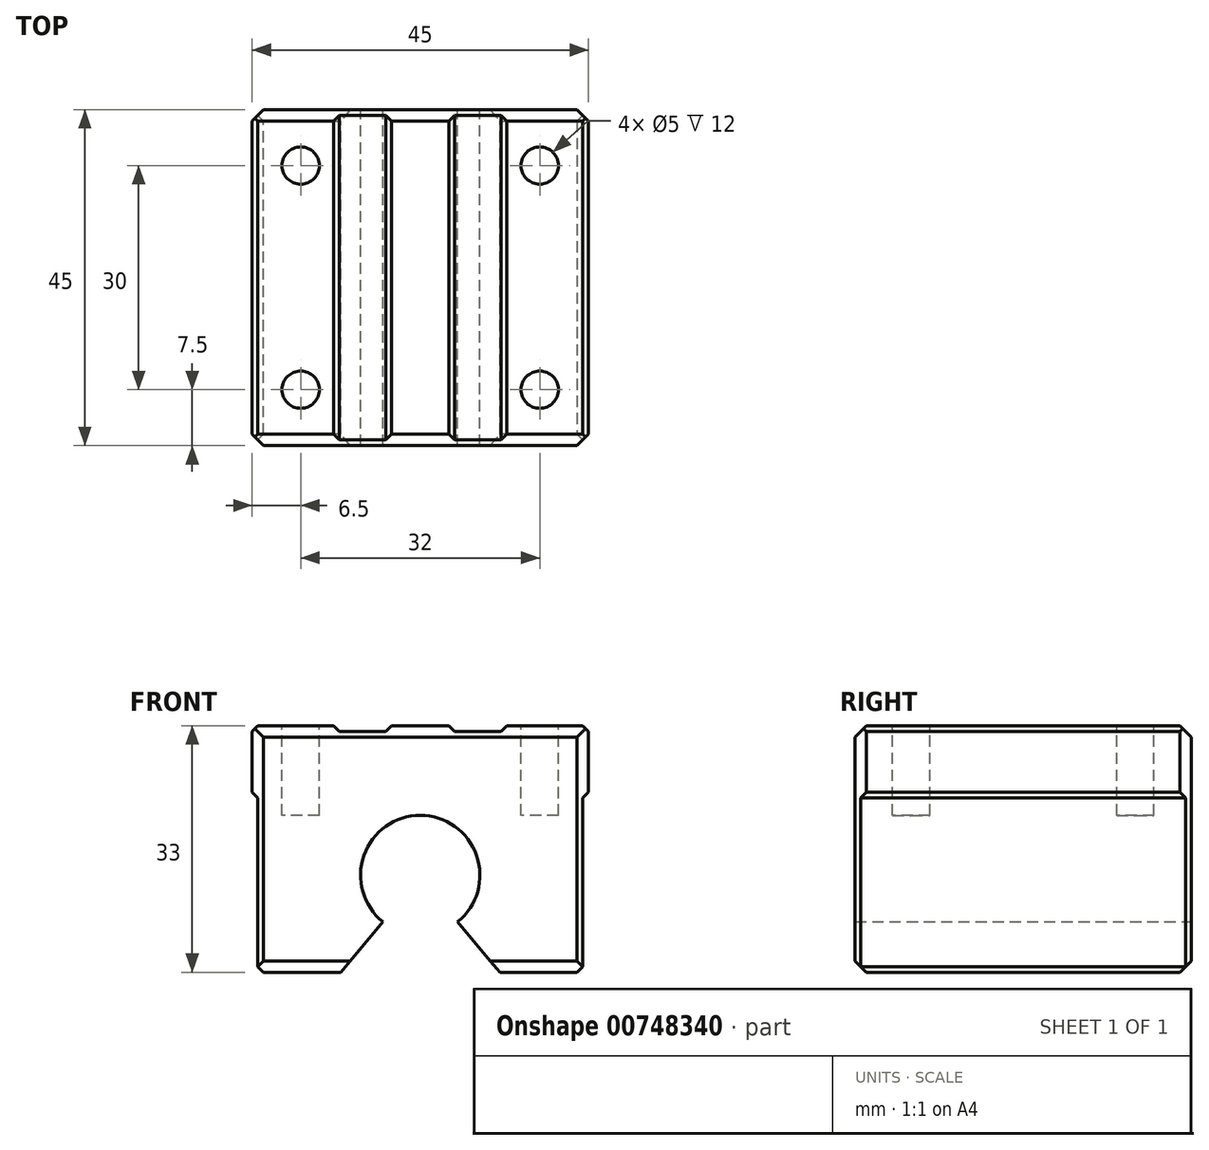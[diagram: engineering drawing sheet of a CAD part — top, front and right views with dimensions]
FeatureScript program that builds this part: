
annotation { "Feature Type Name" : "Feature", "Feature Type Description" : "" }
export const myFeature = defineFeature(function(context is Context, id is Id, definition is map)
    precondition{}
    {
        {
            var Q0;
            Q0=qCreatedBy(makeId("Front.planeOp"),FACE);
            var sketch = newSketch(context, id + "F0", { "sketchPlane" : qUnion([Q0])});
            skPoint(sketch, "E0.middle", {"position": v(0, 0) * mm});
            skLineSegment(sketch, "E1", {"start": v(-22.5, 15.23) * mm, "end": v(-22.5, 7.5) * mm});
            skLineSegment(sketch, "E2", {"start": v(-21.74, 6.82) * mm, "end": v(-21.74, -15.23) * mm});
            skLineSegment(sketch, "E3", {"start": v(-21.23, 16.5) * mm, "end": v(-11.72, 16.5) * mm});
            skLineSegment(sketch, "E4", {"start": v(-10.83, 15.74) * mm, "end": v(-4.58, 15.74) * mm});
            skLineSegment(sketch, "E5", {"start": v(-3.62, 16.5) * mm, "end": v(0, 16.5) * mm});
            skLineSegment(sketch, "E6", {"start": v(0, 16.5) * mm, "end": v(0, -16.5) * mm, "construction": true});
            skLineSegment(sketch, "E7.0", {"start": v(-5, 16.5) * mm, "end": v(-5, -16.5) * mm, "construction": true});
            skLineSegment(sketch, "E8.0", {"start": v(0, -3.5) * mm, "end": v(-21.23, -3.5) * mm, "construction": true});
            skLineSegment(sketch, "E9", {"start": v(-10.67, -16.5) * mm, "end": v(-5, -9.74) * mm});
            skLineSegment(sketch, "E10", {"start": v(0, 16.5) * mm, "end": v(0, 4.5) * mm});
            skArc(sketch, "E11", {"start": v(0, 4.5) * mm, "mid": v(-7.53, -0.86) * mm, "end": v(-5, -9.74) * mm});
            skLineSegment(sketch, "E12", {"start": v(-22.5, 7.5) * mm, "end": v(-22.5, 6.82) * mm});
            skLineSegment(sketch, "E13", {"start": v(-22.5, 6.82) * mm, "end": v(-21.74, 6.82) * mm});
            skLineSegment(sketch, "E14", {"start": v(-21.74, -15.23) * mm, "end": v(-21.74, -16.5) * mm});
            skLineSegment(sketch, "E15", {"start": v(-21.74, -16.5) * mm, "end": v(-20.53, -16.5) * mm});
            skLineSegment(sketch, "E16", {"start": v(-22.5, 15.23) * mm, "end": v(-22.5, 16.5) * mm});
            skLineSegment(sketch, "E17", {"start": v(-22.5, 16.5) * mm, "end": v(-21.23, 16.5) * mm});
            skLineSegment(sketch, "E18", {"start": v(-10.83, 15.74) * mm, "end": v(-10.83, 16.5) * mm});
            skLineSegment(sketch, "E19", {"start": v(-10.83, 16.5) * mm, "end": v(-11.72, 16.5) * mm});
            skLineSegment(sketch, "E20", {"start": v(-4.58, 15.74) * mm, "end": v(-4.58, 16.5) * mm});
            skLineSegment(sketch, "E21", {"start": v(-4.58, 16.5) * mm, "end": v(-3.62, 16.5) * mm});
            skLineSegment(sketch, "E22.MirrorCS", {"start": v(3.62, 16.5) * mm, "end": v(0, 16.5) * mm});
            skLineSegment(sketch, "E23.MirrorCS", {"start": v(4.58, 16.5) * mm, "end": v(3.62, 16.5) * mm});
            skLineSegment(sketch, "E24.MirrorCS", {"start": v(4.58, 15.74) * mm, "end": v(4.58, 16.5) * mm});
            skLineSegment(sketch, "E25.MirrorCS", {"start": v(10.83, 15.74) * mm, "end": v(4.58, 15.74) * mm});
            skLineSegment(sketch, "E26.MirrorCS", {"start": v(10.83, 15.74) * mm, "end": v(10.83, 16.5) * mm});
            skLineSegment(sketch, "E27.MirrorCS", {"start": v(10.83, 16.5) * mm, "end": v(11.72, 16.5) * mm});
            skLineSegment(sketch, "E28.MirrorCS", {"start": v(21.23, 16.5) * mm, "end": v(11.72, 16.5) * mm});
            skLineSegment(sketch, "E29.MirrorCS", {"start": v(22.5, 16.5) * mm, "end": v(21.23, 16.5) * mm});
            skLineSegment(sketch, "E30.MirrorCS", {"start": v(22.5, 15.23) * mm, "end": v(22.5, 16.5) * mm});
            skLineSegment(sketch, "E31.MirrorCS", {"start": v(22.5, 15.23) * mm, "end": v(22.5, 7.5) * mm});
            skLineSegment(sketch, "E32.MirrorCS", {"start": v(22.5, 7.5) * mm, "end": v(22.5, 6.82) * mm});
            skLineSegment(sketch, "E33.MirrorCS", {"start": v(22.5, 6.82) * mm, "end": v(21.74, 6.82) * mm});
            skLineSegment(sketch, "E34.MirrorCS", {"start": v(21.74, 6.82) * mm, "end": v(21.74, -15.23) * mm});
            skLineSegment(sketch, "E35.MirrorCS", {"start": v(21.74, -15.23) * mm, "end": v(21.74, -16.5) * mm});
            skLineSegment(sketch, "E36.MirrorCS", {"start": v(21.74, -16.5) * mm, "end": v(20.53, -16.5) * mm});
            skLineSegment(sketch, "E37", {"start": v(-20.53, -16.5) * mm, "end": v(-10.67, -16.5) * mm});
            skLineSegment(sketch, "E38.MirrorCS", {"start": v(20.53, -16.5) * mm, "end": v(10.67, -16.5) * mm});
            skLineSegment(sketch, "E39.MirrorCS", {"start": v(10.67, -16.5) * mm, "end": v(5, -9.74) * mm});
            skArc(sketch, "E40.MirrorCS", {"start": v(0, 4.5) * mm, "mid": v(7.53, -0.86) * mm, "end": v(5, -9.74) * mm});
            skSolve(sketch);
        }
        {
            var Q0;
            Q0=makeQuery(id+"F0.imprint","IMPRINT",FACE,{"disambiguationData":[TD([[makeQuery(id+"F0.imprint","IMPRINT",EDGE,{"derivedFrom":sQuery(id+"F0.wireOp",EDGE,"E10")}),1.0]])]});
            var Q1;
            Q1=makeQuery(id+"F0.imprint","IMPRINT",FACE,{"disambiguationData":[TD([[makeQuery(id+"F0.imprint","IMPRINT",EDGE,{"derivedFrom":sQuery(id+"F0.wireOp",EDGE,"E1")}),1.0]])]});
            extrude(context, id + "F1", {"entities" : qUnion([Q0, Q1]), "depth" : 45 * mm, "offsetDistance" : 25.4 * mm});
        }
        {
            var Q0;
            Q0=makeQuery(id+"F1.opExtrude","SWEPT_EDGE",EDGE,{"disambiguationData":[OSD([sQuery(id+"F0.wireOp",EDGE,"E16"),sQuery(id+"F0.wireOp",EDGE,"E17")])]});
            chamfer(context, id + "F2", {"entities" : qUnion([Q0]), "chamferType" : ChamferType.OFFSET_ANGLE, "width" : 0.76 * mm, "oppositeDirection" : false, "angle" : 45 * degree, "tangentPropagation" : true});
        }
        {
            var Q0;
            Q0=makeQuery(id+"F1.opExtrude","SWEPT_EDGE",EDGE,{"disambiguationData":[OSD([sQuery(id+"F0.wireOp",EDGE,"E18"),sQuery(id+"F0.wireOp",EDGE,"E19")])]});
            var Q1;
            Q1=makeQuery(id+"F1.opExtrude","SWEPT_EDGE",EDGE,{"disambiguationData":[OSD([sQuery(id+"F0.wireOp",EDGE,"E20"),sQuery(id+"F0.wireOp",EDGE,"E21")])]});
            var Q2;
            Q2=makeQuery(id+"F1.opExtrude","SWEPT_EDGE",EDGE,{"disambiguationData":[OSD([sQuery(id+"F0.wireOp",EDGE,"E23.MirrorCS"),sQuery(id+"F0.wireOp",EDGE,"E24.MirrorCS")])]});
            var Q3;
            Q3=makeQuery(id+"F1.opExtrude","SWEPT_EDGE",EDGE,{"disambiguationData":[OSD([sQuery(id+"F0.wireOp",EDGE,"E26.MirrorCS"),sQuery(id+"F0.wireOp",EDGE,"E27.MirrorCS")])]});
            var Q4;
            Q4=makeQuery(id+"F1.opExtrude","SWEPT_EDGE",EDGE,{"disambiguationData":[OSD([sQuery(id+"F0.wireOp",EDGE,"E29.MirrorCS"),sQuery(id+"F0.wireOp",EDGE,"E30.MirrorCS")])]});
            var Q5;
            Q5=makeQuery(id+"F1.opExtrude","SWEPT_EDGE",EDGE,{"disambiguationData":[OSD([sQuery(id+"F0.wireOp",EDGE,"E32.MirrorCS"),sQuery(id+"F0.wireOp",EDGE,"E33.MirrorCS")])]});
            var Q6;
            Q6=makeQuery(id+"F1.opExtrude","SWEPT_EDGE",EDGE,{"disambiguationData":[OSD([sQuery(id+"F0.wireOp",EDGE,"E35.MirrorCS"),sQuery(id+"F0.wireOp",EDGE,"E36.MirrorCS")])]});
            var Q7;
            Q7=makeQuery(id+"F1.opExtrude","SWEPT_EDGE",EDGE,{"disambiguationData":[OSD([sQuery(id+"F0.wireOp",EDGE,"E12"),sQuery(id+"F0.wireOp",EDGE,"E13")])]});
            var Q8;
            Q8=makeQuery(id+"F1.opExtrude","SWEPT_EDGE",EDGE,{"disambiguationData":[OSD([sQuery(id+"F0.wireOp",EDGE,"E14"),sQuery(id+"F0.wireOp",EDGE,"E15")])]});
            chamfer(context, id + "F3", {"entities" : qUnion([Q0, Q1, Q2, Q3, Q4, Q5, Q6, Q7, Q8]), "width" : 0.76 * mm, "tangentPropagation" : true});
        }
        {
            var Q0;
            Q0=makeQuery(id+"F1.opExtrude","CAP_EDGE",EDGE,{"disambiguationData":[OSD([sQuery(id+"F0.wireOp",EDGE,"E3"),sQuery(id+"F0.wireOp",EDGE,"E17"),sQuery(id+"F0.wireOp",EDGE,"E19")])],"isStart":false});
            var Q1;
            Q1=makeQuery(id+"F1.opExtrude","CAP_EDGE",EDGE,{"disambiguationData":[OSD([sQuery(id+"F0.wireOp",EDGE,"E1"),sQuery(id+"F0.wireOp",EDGE,"E12"),sQuery(id+"F0.wireOp",EDGE,"E16")])],"isStart":false});
            chamfer(context, id + "F4", {"entities" : qUnion([Q0, Q1]), "width" : 1.52 * mm, "tangentPropagation" : true});
        }
        {
            var Q0;
            Q0=makeQuery(id+"F1.opExtrude","CAP_EDGE",EDGE,{"disambiguationData":[OSD([sQuery(id+"F0.wireOp",EDGE,"E30.MirrorCS"),sQuery(id+"F0.wireOp",EDGE,"E31.MirrorCS"),sQuery(id+"F0.wireOp",EDGE,"E32.MirrorCS")])],"isStart":false});
            var Q1;
            Q1=makeQuery(id+"F1.opExtrude","CAP_EDGE",EDGE,{"disambiguationData":[OSD([sQuery(id+"F0.wireOp",EDGE,"E36.MirrorCS"),sQuery(id+"F0.wireOp",EDGE,"E38.MirrorCS")])],"isStart":false});
            var Q2;
            Q2=makeQuery(id+"F1.opExtrude","CAP_EDGE",EDGE,{"disambiguationData":[OSD([sQuery(id+"F0.wireOp",EDGE,"E15"),sQuery(id+"F0.wireOp",EDGE,"E37")])],"isStart":false});
            chamfer(context, id + "F5", {"entities" : qUnion([Q0, Q1, Q2]), "width" : 1.52 * mm, "tangentPropagation" : true});
        }
        {
            var Q0;
            Q0=makeQuery(id+"F1.opExtrude","CAP_EDGE",EDGE,{"disambiguationData":[OSD([sQuery(id+"F0.wireOp",EDGE,"E27.MirrorCS"),sQuery(id+"F0.wireOp",EDGE,"E28.MirrorCS"),sQuery(id+"F0.wireOp",EDGE,"E29.MirrorCS")])],"isStart":true});
            var Q1;
            Q1=makeQuery(id+"F1.opExtrude","CAP_EDGE",EDGE,{"disambiguationData":[OSD([sQuery(id+"F0.wireOp",EDGE,"E30.MirrorCS"),sQuery(id+"F0.wireOp",EDGE,"E31.MirrorCS"),sQuery(id+"F0.wireOp",EDGE,"E32.MirrorCS")])],"isStart":true});
            chamfer(context, id + "F6", {"entities" : qUnion([Q0, Q1]), "width" : 1.52 * mm, "tangentPropagation" : true});
        }
        {
            var Q0;
            Q0=makeQuery(id+"F1.opExtrude","CAP_EDGE",EDGE,{"disambiguationData":[OSD([sQuery(id+"F0.wireOp",EDGE,"E1"),sQuery(id+"F0.wireOp",EDGE,"E12"),sQuery(id+"F0.wireOp",EDGE,"E16")])],"isStart":true});
            var Q1;
            Q1=makeQuery(id+"F1.opExtrude","CAP_EDGE",EDGE,{"disambiguationData":[OSD([sQuery(id+"F0.wireOp",EDGE,"E15"),sQuery(id+"F0.wireOp",EDGE,"E37")])],"isStart":true});
            var Q2;
            Q2=makeQuery(id+"F1.opExtrude","CAP_EDGE",EDGE,{"disambiguationData":[OSD([sQuery(id+"F0.wireOp",EDGE,"E36.MirrorCS"),sQuery(id+"F0.wireOp",EDGE,"E38.MirrorCS")])],"isStart":true});
            chamfer(context, id + "F7", {"entities" : qUnion([Q0, Q1, Q2]), "width" : 1.52 * mm, "tangentPropagation" : true});
        }
        {
            var Q0;
            Q0=makeQuery(id+"F1.opExtrude","SWEPT_FACE",FACE,{"disambiguationData":[OSD([sQuery(id+"F0.wireOp",EDGE,"E5"),sQuery(id+"F0.wireOp",EDGE,"E21"),sQuery(id+"F0.wireOp",EDGE,"E22.MirrorCS"),sQuery(id+"F0.wireOp",EDGE,"E23.MirrorCS")])]});
            var sketch = newSketch(context, id + "F8", { "sketchPlane" : qUnion([Q0])});
            skLineSegment(sketch, "E41.bottom", {"start": v(-16, -7.5) * mm, "end": v(16, -7.5) * mm, "construction": true});
            skLineSegment(sketch, "E41.top", {"start": v(-16, -37.5) * mm, "end": v(16, -37.5) * mm, "construction": true});
            skLineSegment(sketch, "E41.left", {"start": v(-16, -7.5) * mm, "end": v(-16, -37.5) * mm, "construction": true});
            skLineSegment(sketch, "E41.right", {"start": v(16, -7.5) * mm, "end": v(16, -37.5) * mm, "construction": true});
            skPoint(sketch, "E41.middle", {"position": v(0, -22.5) * mm});
            skPoint(sketch, "E41.middle.positionSnap0", {"position": v(3.82, -22.5) * mm});
            skPoint(sketch, "E41.middle.positionSnap1", {"position": v(0, -1.52) * mm});
            skPoint(sketch, "E41.centerSnap0", {"position": v(3.82, -22.5) * mm});
            skPoint(sketch, "E41.centerSnap1", {"position": v(0, -1.52) * mm});
            skCircle(sketch, "E42", {"center": v(16, -37.5) * mm, "radius": 2.5 * mm});
            skCircle(sketch, "E43", {"center": v(16, -7.5) * mm, "radius": 2.5 * mm});
            skCircle(sketch, "E44", {"center": v(-16, -7.5) * mm, "radius": 2.5 * mm});
            skCircle(sketch, "E45", {"center": v(-16, -37.5) * mm, "radius": 2.5 * mm});
            skSolve(sketch);
        }
        {
            var Q0;
            Q0 = qSketchRegion(id + "F8", true);
            extrude(context, id + "F9", {"entities" : qUnion([Q0]), "operationType" : NewBodyOperationType.REMOVE, "oppositeDirection" : true, "depth" : 12 * mm, "offsetDistance" : 25.4 * mm});
        }
    });
